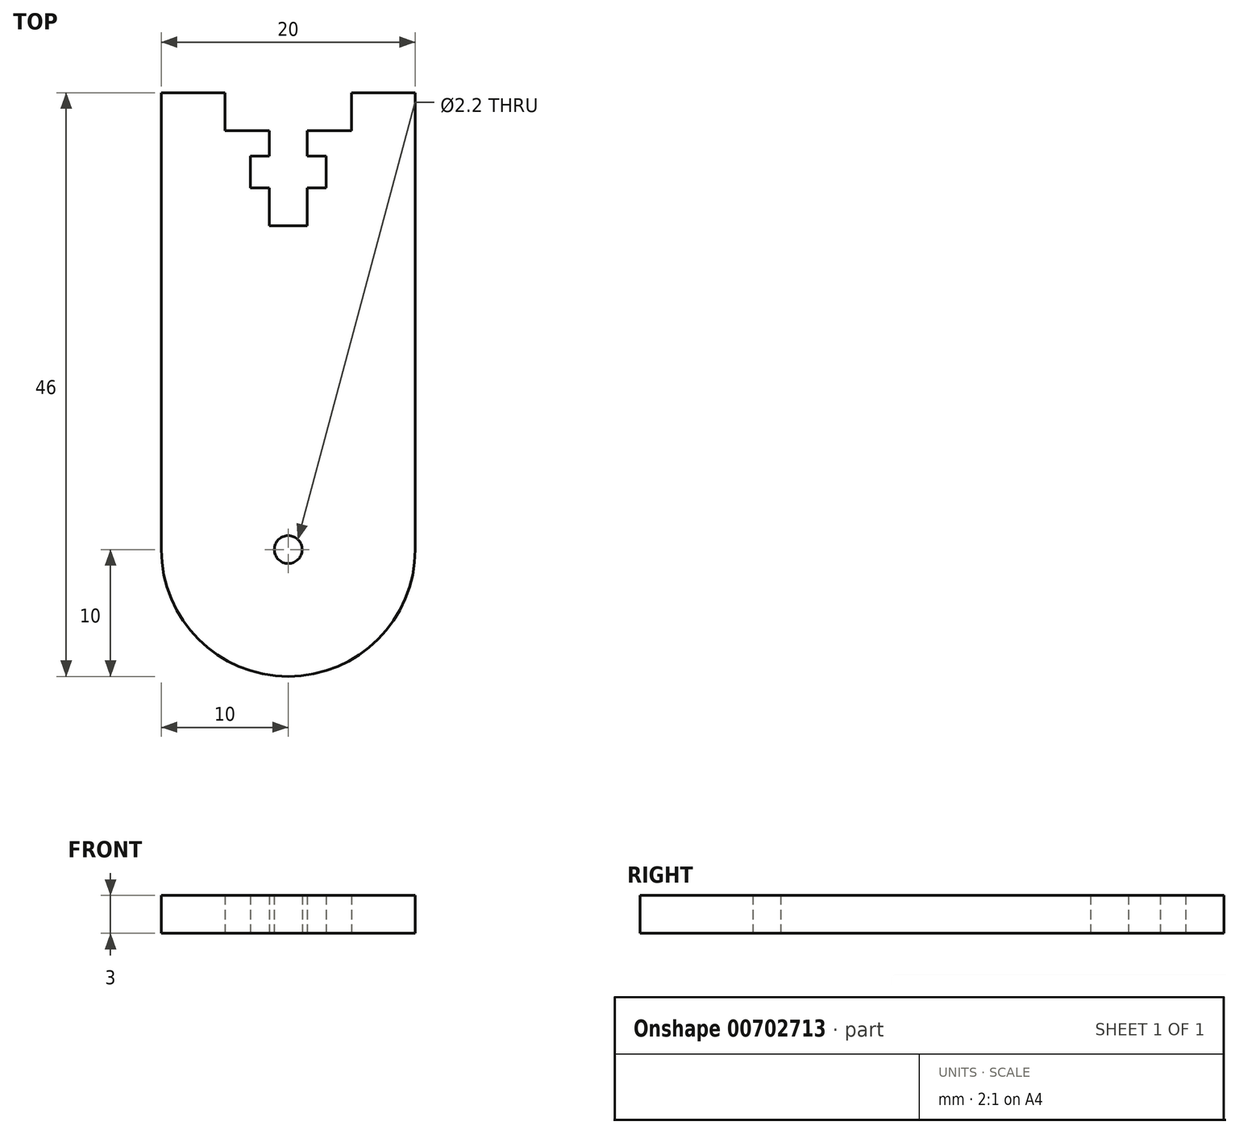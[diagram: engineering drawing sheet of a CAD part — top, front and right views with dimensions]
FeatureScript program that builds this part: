
annotation { "Feature Type Name" : "Feature", "Feature Type Description" : "" }
export const myFeature = defineFeature(function(context is Context, id is Id, definition is map)
    precondition{}
    {
        {
            var Q0;
            Q0=qCreatedBy(makeId("Top.planeOp"),FACE);
            var sketch = newSketch(context, id + "F0", { "sketchPlane" : qUnion([Q0])});
            skLineSegment(sketch, "E0.bottom", {"start": v(5, 0) * mm, "end": v(8.5, 0) * mm});
            skLineSegment(sketch, "E0.left", {"start": v(0, 0) * mm, "end": v(0, -33) * mm});
            skLineSegment(sketch, "E0.right", {"start": v(20, 0) * mm, "end": v(20, -33) * mm});
            skArc(sketch, "E1", {"start": v(0, -33) * mm, "mid": v(10, -43) * mm, "end": v(20, -33) * mm});
            skLineSegment(sketch, "E2", {"start": v(10, 0) * mm, "end": v(10, -7.55) * mm, "construction": true});
            skLineSegment(sketch, "E3", {"start": v(8.5, 0) * mm, "end": v(8.5, -2) * mm});
            skLineSegment(sketch, "E4", {"start": v(8.5, -2) * mm, "end": v(7, -2) * mm});
            skLineSegment(sketch, "E5", {"start": v(7, -2) * mm, "end": v(7, -4.5) * mm});
            skLineSegment(sketch, "E6", {"start": v(7, -4.5) * mm, "end": v(8.5, -4.5) * mm});
            skLineSegment(sketch, "E7", {"start": v(8.5, -4.5) * mm, "end": v(8.5, -7.5) * mm});
            skLineSegment(sketch, "E8", {"start": v(8.5, -7.5) * mm, "end": v(10, -7.5) * mm});
            skLineSegment(sketch, "E9.MirrorCS", {"start": v(11.5, -4.5) * mm, "end": v(11.5, -7.5) * mm});
            skLineSegment(sketch, "E10.MirrorCS", {"start": v(13, -4.5) * mm, "end": v(11.5, -4.5) * mm});
            skLineSegment(sketch, "E11.MirrorCS", {"start": v(13, -2) * mm, "end": v(13, -4.5) * mm});
            skLineSegment(sketch, "E12.MirrorCS", {"start": v(11.5, -2) * mm, "end": v(13, -2) * mm});
            skLineSegment(sketch, "E13.MirrorCS", {"start": v(11.5, -7.5) * mm, "end": v(10, -7.5) * mm});
            skLineSegment(sketch, "E14.MirrorCS", {"start": v(11.5, 0) * mm, "end": v(11.5, -2) * mm});
            skCircle(sketch, "E15", {"center": v(10, -33) * mm, "radius": 1.1 * mm});
            skLineSegment(sketch, "E16", {"start": v(20, 0) * mm, "end": v(20, 3) * mm});
            skLineSegment(sketch, "E17", {"start": v(20, 3) * mm, "end": v(15, 3) * mm});
            skLineSegment(sketch, "E18", {"start": v(15, 3) * mm, "end": v(15, 0) * mm});
            skLineSegment(sketch, "E19.MirrorCS", {"start": v(0, 3) * mm, "end": v(5, 3) * mm});
            skLineSegment(sketch, "E20.MirrorCS", {"start": v(5, 3) * mm, "end": v(5, 0) * mm});
            skLineSegment(sketch, "E21.MirrorCS", {"start": v(0, 0) * mm, "end": v(0, 3) * mm});
            skLineSegment(sketch, "E22.trimOffspring", {"start": v(11.5, 0) * mm, "end": v(15, 0) * mm});
            skSolve(sketch);
        }
        {
            var Q0;
            Q0=makeQuery(id+"F0.imprint","IMPRINT",FACE,{"disambiguationData":[TD([[makeQuery(id+"F0.imprint","IMPRINT",EDGE,{"derivedFrom":sQuery(id+"F0.wireOp",EDGE,"E0.bottom")}),-1.0]])]});
            extrude(context, id + "F1", {"entities" : qUnion([Q0]), "depth" : 3 * mm, "offsetDistance" : 25.4 * mm});
        }
    });
